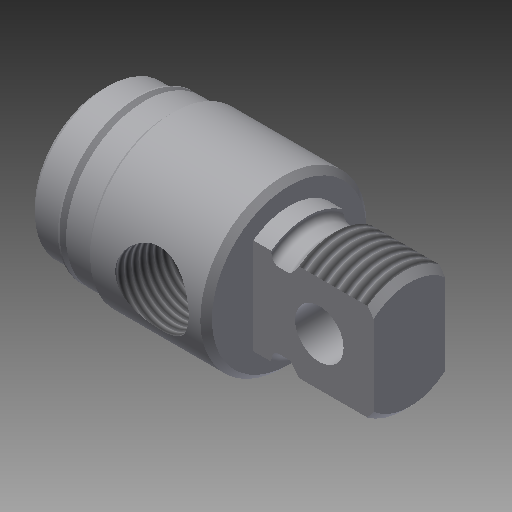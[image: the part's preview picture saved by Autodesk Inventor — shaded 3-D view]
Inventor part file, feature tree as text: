
AUTODESK INVENTOR PART (.ipt)
format: ipt  version: 2019 (Build 230136000, 136)  size: 348,672 bytes
history: native  units: in
note: dims shown in document units (in); Inventor stores cm internally (conversion verified against a paired STEP export)
features: other x154, sketch x7, revolve x4, thread x2, extrude x2, hole x1
ambient origin geometry x8: Origin, YZ Plane, XZ Plane, XY Plane, X Axis, Y Axis, Z Axis, Center Point
bodies: Solid1 (feature_tree)
feature tree (170):
  revolve  "Revolution1"  Angle=360.0deg
  revolve  "Revolution2"  [1 undecoded]
  thread  "Thread1"  [1 undecoded]
  extrude  "Extrusion1"  TaperAngle=360.0deg  [1 undecoded]
  hole  "Hole1"  [1 undecoded]
  revolve  "Revolution3"  [1 undecoded]
  thread  "Thread2"  [1 undecoded]
  revolve  "Revolution4"  [1 undecoded]
  extrude  "Extrusion2"  [1 undecoded]
  other  "1_XY"
  other  "1_YZ"
  other  "1_ZX"
  other  "1_X"
  other  "1_Y"
  other  "1_Z"
  other  "1_Center"
  other  "c1_XY"
  other  "c1_YZ"
  other  "c1_ZX"
  other  "c1_X"
  other  "c1_Y"
  other  "c1_Z"
  other  "c1_Center"
  other  "c2_XY"
  other  "c2_YZ"
  other  "c2_ZX"
  other  "c2_X"
  other  "c2_Y"
  other  "c2_Z"
  other  "c2_Center"
  other  "cc1_XY"
  other  "cc1_YZ"
  other  "cc1_ZX"
  other  "cc1_X"
  other  "cc1_Y"
  other  "cc1_Z"
  other  "cc1_Center"
  other  "cc2_XY"
  other  "cc2_YZ"
  other  "cc2_ZX"
  other  "cc2_X"
  other  "cc2_Y"
  other  "cc2_Z"
  other  "cc2_Center"
  other  "lovra1_XY"
  other  "lovra1_YZ"
  other  "lovra1_ZX"
  other  "lovra1_X"
  other  "lovra1_Y"
  other  "lovra1_Z"
  other  "lovra1_Center"
  other  "lovra2_XY"
  other  "lovra2_YZ"
  other  "lovra2_ZX"
  other  "lovra2_X"
  other  "lovra2_Y"
  other  "lovra2_Z"
  other  "lovra2_Center"
  other  "lovra21_XY"
  other  "lovra21_YZ"
  other  "lovra21_ZX"
  other  "lovra21_X"
  other  "lovra21_Y"
  other  "lovra21_Z"
  other  "lovra21_Center"
  other  "lovra22_XY"
  other  "lovra22_YZ"
  other  "lovra22_ZX"
  other  "lovra22_X"
  other  "lovra22_Y"
  other  "lovra22_Z"
  other  "lovra22_Center"
  other  "lovra3_XY"
  other  "lovra3_YZ"
  other  "lovra3_ZX"
  other  "lovra3_X"
  other  "lovra3_Y"
  other  "lovra3_Z"
  other  "lovra3_Center"
  other  "olen_XY"
  other  "olen_YZ"
  other  "olen_ZX"
  other  "olen_X"
  other  "olen_Y"
  other  "olen_Z"
  other  "olen_Center"
  other  "p1_XY"
  other  "p1_YZ"
  other  "p1_ZX"
  other  "p1_X"
  other  "p1_Y"
  other  "p1_Z"
  other  "p1_Center"
  other  "p2_XY"
  other  "p2_YZ"
  other  "p2_ZX"
  other  "p2_X"
  other  "p2_Y"
  other  "p2_Z"
  other  "p2_Center"
  other  "port_XY"
  other  "port_YZ"
  other  "port_ZX"
  other  "port_X"
  other  "port_Y"
  other  "port_Z"
  other  "port_Center"
  other  "port2_XY"
  other  "port2_YZ"
  other  "port2_ZX"
  other  "port2_X"
  other  "port2_Y"
  other  "port2_Z"
  other  "port2_Center"
  other  "thd1_XY"
  other  "thd1_YZ"
  other  "thd1_ZX"
  other  "thd1_X"
  other  "thd1_Y"
  other  "thd1_Z"
  other  "thd1_Center"
  other  "thd2_XY"
  other  "thd2_YZ"
  other  "thd2_ZX"
  other  "thd2_X"
  other  "thd2_Y"
  other  "thd2_Z"
  other  "thd2_Center"
  other  "to_mounting_bracket_XY"
  other  "to_mounting_bracket_YZ"
  other  "to_mounting_bracket_ZX"
  other  "to_mounting_bracket_X"
  other  "to_mounting_bracket_Y"
  other  "to_mounting_bracket_Z"
  other  "to_mounting_bracket_Center"
  other  "to_nut_XY"
  other  "to_nut_YZ"
  other  "to_nut_ZX"
  other  "to_nut_X"
  other  "to_nut_Y"
  other  "to_nut_Z"
  other  "to_nut_Center"
  other  "to_pin_XY"
  other  "to_pin_YZ"
  other  "to_pin_ZX"
  other  "to_pin_X"
  other  "to_pin_Y"
  other  "to_pin_Z"
  other  "to_pin_Center"
  other  "to_screw_XY"
  other  "to_screw_YZ"
  other  "to_screw_ZX"
  other  "to_screw_X"
  other  "to_screw_Y"
  other  "to_screw_Z"
  other  "to_screw_Center"
  other  "to_tube_XY"
  other  "to_tube_YZ"
  other  "to_tube_ZX"
  other  "to_tube_X"
  other  "to_tube_Y"
  other  "to_tube_Z"
  other  "to_tube_Center"
  sketch  "Sketch_8"  dims[d2=0.3547in d3=0.0in d4=0.625in d5=0.0in]
  sketch  "Sketch_15"  dims[d14=0.3021in d15=0.0in d16=360.0deg]
  sketch  "Sketch_9"  dims[d6=0.312in d7=0.75in d8=0.375in d9=0.25in d10=0.5635in d11=0.9284in d12=120.0deg d13=360.0deg]
  sketch  "Sketch4"  dims[d0=360.0deg d1=360.0deg]
  sketch  "Sketch_68"
  sketch  "Sketch_24"  dims[d17=0.5587in d18=0.0in]
  sketch  "Sketch_43"  dims[d19=0.0in d20=0.0in d21=0.0in d22=0.0in d23=0.0in d24=0.0in d25=0.0in d26=0.0in]
note: 8 required parameter values undecoded (feature->parameter linkage not recoverable at this tier; creation-order binding heuristic only, values carry confidence <= 0.55)